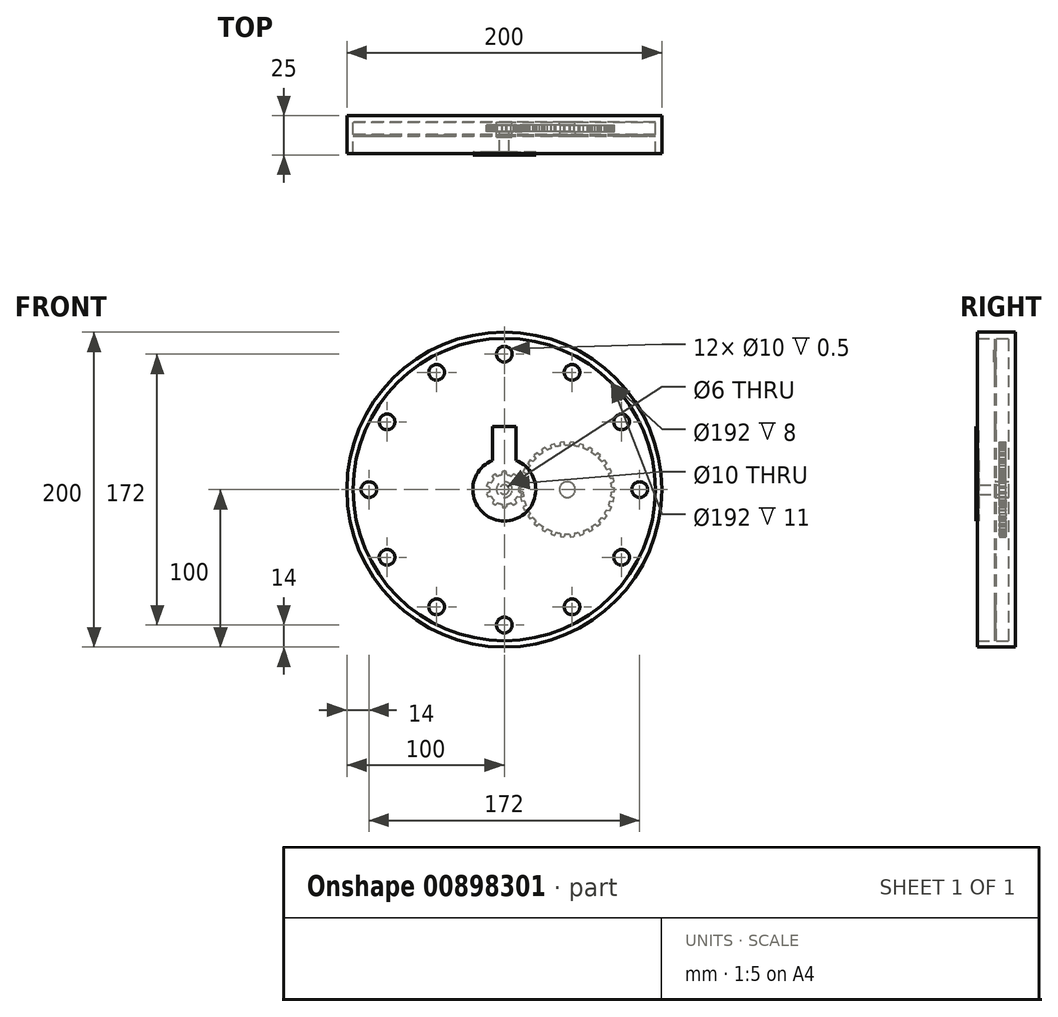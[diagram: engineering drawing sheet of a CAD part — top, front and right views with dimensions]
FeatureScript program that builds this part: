
annotation { "Feature Type Name" : "Feature", "Feature Type Description" : "" }
export const myFeature = defineFeature(function(context is Context, id is Id, definition is map)
    precondition{}
    {
        {
            var Q0;
            Q0=qCreatedBy(makeId("Front.planeOp"),FACE);
            var sketch = newSketch(context, id + "F0", { "sketchPlane" : qUnion([Q0])});
            skCircle(sketch, "E0", {"center": v(0, 0) * mm, "radius": 100 * mm});
            skSolve(sketch);
        }
        {
            var Q0;
            Q0=makeQuery(id+"F0.imprint","IMPRINT",FACE,{"disambiguationData":[TD([[makeQuery(id+"F0.imprint","IMPRINT",EDGE,{"derivedFrom":sQuery(id+"F0.wireOp",EDGE,"E0")}),1.0]])]});
            extrude(context, id + "F1", {"entities" : qUnion([Q0]), "depth" : 24 * mm, "offsetDistance" : 25 * mm});
        }
        {
            var Q0;
            Q0=makeQuery(id+"F1.opExtrude","CAP_FACE",FACE,{"disambiguationData":[OSD([sQuery(id+"F0.wireOp",EDGE,"E0")])],"isStart":false});
            shell(context, id + "F2", {"entities" : qUnion([Q0]), "thickness" : 4 * mm});
        }
        {
            var Q0;
            Q0=qCreatedBy(makeId("Front.planeOp"),FACE);
            var sketch = newSketch(context, id + "F3", { "sketchPlane" : qUnion([Q0])});
            skCircle(sketch, "E1", {"center": v(40, 0) * mm, "radius": 3 * mm});
            skCircle(sketch, "E2", {"center": v(40, 0) * mm, "radius": 5 * mm});
            skCircle(sketch, "E3", {"center": v(0, 0) * mm, "radius": 3 * mm});
            skCircle(sketch, "E4", {"center": v(0, 0) * mm, "radius": 5 * mm});
            skSolve(sketch);
        }
        {
            var Q0;
            Q0 = qSketchRegion(id + "F3", true);
            extrude(context, id + "F4", {"entities" : qUnion([Q0]), "operationType" : NewBodyOperationType.ADD, "depth" : 6 * mm, "offsetDistance" : 25 * mm});
        }
        {
            var Q0;
            {var subQ0=sQuery(id+"F0.wireOp",EDGE,"E0");Q0=makeQuery(id+"F4.boolean.opBoolean","SPLIT",FACE,{"disambiguationData":[TD([makeQuery(id+"F4.opExtrude","SWEPT_FACE",FACE,{"disambiguationData":[OSD([sQuery(id+"F3.wireOp",EDGE,"E3")])]})])],"derivedFrom":makeQuery(id+"F2.opShell","OFFSET_FACE",FACE,{"disambiguationData":[OSD([subQ0]),TDD([makeQuery(id+"F1.opExtrude","CAP_FACE",FACE,{"disambiguationData":[OSD([subQ0])],"isStart":true})])]})});}
            extrude(context, id + "F5", {"entities" : qUnion([Q0]), "depth" : 19 * mm, "offsetDistance" : 25 * mm});
        }
        {
            var Q0;
            {var subQ0=sQuery(id+"F0.wireOp",EDGE,"E0");Q0=makeQuery(id+"F4.boolean.opBoolean","SPLIT",FACE,{"disambiguationData":[TD([makeQuery(id+"F4.opExtrude","SWEPT_FACE",FACE,{"disambiguationData":[OSD([sQuery(id+"F3.wireOp",EDGE,"E1")])]})])],"derivedFrom":makeQuery(id+"F2.opShell","OFFSET_FACE",FACE,{"disambiguationData":[OSD([subQ0]),TDD([makeQuery(id+"F1.opExtrude","CAP_FACE",FACE,{"disambiguationData":[OSD([subQ0])],"isStart":true})])]})});}
            extrude(context, id + "F6", {"entities" : qUnion([Q0]), "depth" : 8 * mm, "offsetDistance" : 25 * mm});
        }
        {
            var Q0;
            Q0=makeQuery(id+"F4.opExtrude","CAP_FACE",FACE,{"disambiguationData":[OSD([sQuery(id+"F3.wireOp",EDGE,"E3"),sQuery(id+"F3.wireOp",EDGE,"E4")])],"isStart":false});
            var sketch = newSketch(context, id + "F7", { "sketchPlane" : qUnion([Q0])});
            skCircle(sketch, "E5", {"center": v(0, 0) * mm, "radius": 9.38 * mm});
            skLineSegment(sketch, "E6", {"start": v(1.55, 9.25) * mm, "end": v(1.18, 11.38) * mm});
            skLineSegment(sketch, "E7", {"start": v(1.18, 11.38) * mm, "end": v(0, 11.38) * mm});
            skLineSegment(sketch, "E8.MirrorCS", {"start": v(-1.18, 11.38) * mm, "end": v(0, 11.38) * mm});
            skLineSegment(sketch, "E9.MirrorCS", {"start": v(-1.55, 9.25) * mm, "end": v(-1.18, 11.38) * mm});
            skLineSegment(sketch, "E10.1.0", {"start": v(-6.7, 6.57) * mm, "end": v(-7.64, 8.51) * mm});
            skLineSegment(sketch, "E10.1.1", {"start": v(-7.64, 8.51) * mm, "end": v(-6.69, 9.2) * mm});
            skLineSegment(sketch, "E10.1.2", {"start": v(-5.73, 9.9) * mm, "end": v(-6.69, 9.2) * mm});
            skLineSegment(sketch, "E10.1.3", {"start": v(-4.18, 8.4) * mm, "end": v(-5.73, 9.9) * mm});
            skLineSegment(sketch, "E10.2.0", {"start": v(-9.27, 1.38) * mm, "end": v(-11.18, 2.4) * mm});
            skLineSegment(sketch, "E10.2.1", {"start": v(-11.18, 2.4) * mm, "end": v(-10.82, 3.52) * mm});
            skLineSegment(sketch, "E10.2.2", {"start": v(-10.45, 4.64) * mm, "end": v(-10.82, 3.52) * mm});
            skLineSegment(sketch, "E10.2.3", {"start": v(-8.31, 4.33) * mm, "end": v(-10.45, 4.64) * mm});
            skLineSegment(sketch, "E10.3.0", {"start": v(-8.31, -4.33) * mm, "end": v(-10.45, -4.64) * mm});
            skLineSegment(sketch, "E10.3.1", {"start": v(-10.45, -4.64) * mm, "end": v(-10.82, -3.52) * mm});
            skLineSegment(sketch, "E10.3.2", {"start": v(-11.18, -2.4) * mm, "end": v(-10.82, -3.52) * mm});
            skLineSegment(sketch, "E10.3.3", {"start": v(-9.27, -1.38) * mm, "end": v(-11.18, -2.4) * mm});
            skLineSegment(sketch, "E10.4.0", {"start": v(-4.18, -8.4) * mm, "end": v(-5.73, -9.9) * mm});
            skLineSegment(sketch, "E10.4.1", {"start": v(-5.73, -9.9) * mm, "end": v(-6.69, -9.2) * mm});
            skLineSegment(sketch, "E10.4.2", {"start": v(-7.64, -8.51) * mm, "end": v(-6.69, -9.2) * mm});
            skLineSegment(sketch, "E10.4.3", {"start": v(-6.7, -6.57) * mm, "end": v(-7.64, -8.51) * mm});
            skLineSegment(sketch, "E10.5.0", {"start": v(1.55, -9.25) * mm, "end": v(1.18, -11.38) * mm});
            skLineSegment(sketch, "E10.5.1", {"start": v(1.18, -11.38) * mm, "end": v(0, -11.38) * mm});
            skLineSegment(sketch, "E10.5.2", {"start": v(-1.18, -11.38) * mm, "end": v(0, -11.38) * mm});
            skLineSegment(sketch, "E10.5.3", {"start": v(-1.55, -9.25) * mm, "end": v(-1.18, -11.38) * mm});
            skLineSegment(sketch, "E10.6.0", {"start": v(6.7, -6.57) * mm, "end": v(7.64, -8.51) * mm});
            skLineSegment(sketch, "E10.6.1", {"start": v(7.64, -8.51) * mm, "end": v(6.69, -9.2) * mm});
            skLineSegment(sketch, "E10.6.2", {"start": v(5.73, -9.9) * mm, "end": v(6.69, -9.2) * mm});
            skLineSegment(sketch, "E10.6.3", {"start": v(4.18, -8.4) * mm, "end": v(5.73, -9.9) * mm});
            skLineSegment(sketch, "E10.7.0", {"start": v(9.27, -1.38) * mm, "end": v(11.18, -2.4) * mm});
            skLineSegment(sketch, "E10.7.1", {"start": v(11.18, -2.4) * mm, "end": v(10.82, -3.52) * mm});
            skLineSegment(sketch, "E10.7.2", {"start": v(10.45, -4.64) * mm, "end": v(10.82, -3.52) * mm});
            skLineSegment(sketch, "E10.7.3", {"start": v(8.31, -4.33) * mm, "end": v(10.45, -4.64) * mm});
            skLineSegment(sketch, "E10.8.0", {"start": v(8.31, 4.33) * mm, "end": v(10.45, 4.64) * mm});
            skLineSegment(sketch, "E10.8.1", {"start": v(10.45, 4.64) * mm, "end": v(10.82, 3.52) * mm});
            skLineSegment(sketch, "E10.8.2", {"start": v(11.18, 2.4) * mm, "end": v(10.82, 3.52) * mm});
            skLineSegment(sketch, "E10.8.3", {"start": v(9.27, 1.38) * mm, "end": v(11.18, 2.4) * mm});
            skLineSegment(sketch, "E10.9.0", {"start": v(4.18, 8.4) * mm, "end": v(5.73, 9.9) * mm});
            skLineSegment(sketch, "E10.9.1", {"start": v(5.73, 9.9) * mm, "end": v(6.69, 9.2) * mm});
            skLineSegment(sketch, "E10.9.2", {"start": v(7.64, 8.51) * mm, "end": v(6.69, 9.2) * mm});
            skLineSegment(sketch, "E10.9.3", {"start": v(6.7, 6.57) * mm, "end": v(7.64, 8.51) * mm});
            skSolve(sketch);
        }
        {
            var Q0;
            Q0 = qSketchRegion(id + "F7", true);
            extrude(context, id + "F8", {"entities" : qUnion([Q0]), "operationType" : NewBodyOperationType.ADD, "depth" : 4 * mm, "offsetDistance" : 25 * mm});
        }
        {
            var Q0;
            Q0=makeQuery(id+"F4.opExtrude","CAP_FACE",FACE,{"disambiguationData":[OSD([sQuery(id+"F3.wireOp",EDGE,"E1"),sQuery(id+"F3.wireOp",EDGE,"E2")])],"isStart":false});
            var sketch = newSketch(context, id + "F9", { "sketchPlane" : qUnion([Q0])});
            skCircle(sketch, "E11", {"center": v(40, 0) * mm, "radius": 28.12 * mm});
            skLineSegment(sketch, "E12", {"start": v(11.92, 1.54) * mm, "end": v(9.88, 1.18) * mm});
            skLineSegment(sketch, "E13", {"start": v(9.88, 1.18) * mm, "end": v(9.88, 0) * mm});
            skLineSegment(sketch, "E14.MirrorCS", {"start": v(9.88, -1.18) * mm, "end": v(9.88, 0) * mm});
            skLineSegment(sketch, "E15.MirrorCS", {"start": v(11.92, -1.54) * mm, "end": v(9.88, -1.18) * mm});
            skLineSegment(sketch, "E16.1.0", {"start": v(12.85, -7.34) * mm, "end": v(10.78, -7.42) * mm});
            skLineSegment(sketch, "E16.1.1", {"start": v(12.21, -4.33) * mm, "end": v(10.29, -5.11) * mm});
            skLineSegment(sketch, "E16.1.2", {"start": v(10.29, -5.11) * mm, "end": v(10.53, -6.26) * mm});
            skLineSegment(sketch, "E16.1.3", {"start": v(10.78, -7.42) * mm, "end": v(10.53, -6.26) * mm});
            skLineSegment(sketch, "E16.2.0", {"start": v(14.97, -12.83) * mm, "end": v(12.96, -13.33) * mm});
            skLineSegment(sketch, "E16.2.1", {"start": v(13.72, -10.02) * mm, "end": v(12, -11.18) * mm});
            skLineSegment(sketch, "E16.2.2", {"start": v(12, -11.18) * mm, "end": v(12.48, -12.25) * mm});
            skLineSegment(sketch, "E16.2.3", {"start": v(12.96, -13.33) * mm, "end": v(12.48, -12.25) * mm});
            skLineSegment(sketch, "E16.3.0", {"start": v(18.18, -17.75) * mm, "end": v(16.32, -18.66) * mm});
            skLineSegment(sketch, "E16.3.1", {"start": v(16.38, -15.26) * mm, "end": v(14.94, -16.75) * mm});
            skLineSegment(sketch, "E16.3.2", {"start": v(14.94, -16.75) * mm, "end": v(15.63, -17.7) * mm});
            skLineSegment(sketch, "E16.3.3", {"start": v(16.32, -18.66) * mm, "end": v(15.63, -17.7) * mm});
            skLineSegment(sketch, "E16.4.0", {"start": v(22.35, -21.9) * mm, "end": v(20.72, -23.18) * mm});
            skLineSegment(sketch, "E16.4.1", {"start": v(20.07, -19.84) * mm, "end": v(18.97, -21.6) * mm});
            skLineSegment(sketch, "E16.4.2", {"start": v(18.97, -21.6) * mm, "end": v(19.84, -22.39) * mm});
            skLineSegment(sketch, "E16.4.3", {"start": v(20.72, -23.18) * mm, "end": v(19.84, -22.39) * mm});
            skLineSegment(sketch, "E16.5.0", {"start": v(27.3, -25.09) * mm, "end": v(25.96, -26.68) * mm});
            skLineSegment(sketch, "E16.5.1", {"start": v(24.63, -23.55) * mm, "end": v(23.92, -25.5) * mm});
            skLineSegment(sketch, "E16.5.2", {"start": v(23.92, -25.5) * mm, "end": v(24.94, -26.09) * mm});
            skLineSegment(sketch, "E16.5.3", {"start": v(25.96, -26.68) * mm, "end": v(24.94, -26.09) * mm});
            skLineSegment(sketch, "E16.6.0", {"start": v(32.78, -27.18) * mm, "end": v(31.81, -29.01) * mm});
            skLineSegment(sketch, "E16.6.1", {"start": v(29.86, -26.23) * mm, "end": v(29.57, -28.29) * mm});
            skLineSegment(sketch, "E16.6.2", {"start": v(29.57, -28.29) * mm, "end": v(30.7, -28.65) * mm});
            skLineSegment(sketch, "E16.6.3", {"start": v(31.81, -29.01) * mm, "end": v(30.7, -28.65) * mm});
            skLineSegment(sketch, "E16.7.0", {"start": v(38.6, -28.09) * mm, "end": v(38.02, -30.08) * mm});
            skLineSegment(sketch, "E16.7.1", {"start": v(35.53, -27.77) * mm, "end": v(35.68, -29.84) * mm});
            skLineSegment(sketch, "E16.7.2", {"start": v(35.68, -29.84) * mm, "end": v(36.85, -29.96) * mm});
            skLineSegment(sketch, "E16.7.3", {"start": v(38.02, -30.08) * mm, "end": v(36.85, -29.96) * mm});
            skLineSegment(sketch, "E16.8.0", {"start": v(44.47, -27.77) * mm, "end": v(44.32, -29.84) * mm});
            skLineSegment(sketch, "E16.8.1", {"start": v(41.4, -28.09) * mm, "end": v(41.98, -30.08) * mm});
            skLineSegment(sketch, "E16.8.2", {"start": v(41.98, -30.08) * mm, "end": v(43.15, -29.96) * mm});
            skLineSegment(sketch, "E16.8.3", {"start": v(44.32, -29.84) * mm, "end": v(43.15, -29.96) * mm});
            skLineSegment(sketch, "E16.9.0", {"start": v(50.14, -26.23) * mm, "end": v(50.43, -28.29) * mm});
            skLineSegment(sketch, "E16.9.1", {"start": v(47.22, -27.18) * mm, "end": v(48.19, -29.01) * mm});
            skLineSegment(sketch, "E16.9.2", {"start": v(48.19, -29.01) * mm, "end": v(49.3, -28.65) * mm});
            skLineSegment(sketch, "E16.9.3", {"start": v(50.43, -28.29) * mm, "end": v(49.3, -28.65) * mm});
            skLineSegment(sketch, "E16.10.0", {"start": v(55.37, -23.55) * mm, "end": v(56.08, -25.5) * mm});
            skLineSegment(sketch, "E16.10.1", {"start": v(52.7, -25.09) * mm, "end": v(54.04, -26.68) * mm});
            skLineSegment(sketch, "E16.10.2", {"start": v(54.04, -26.68) * mm, "end": v(55.06, -26.09) * mm});
            skLineSegment(sketch, "E16.10.3", {"start": v(56.08, -25.5) * mm, "end": v(55.06, -26.09) * mm});
            skLineSegment(sketch, "E16.11.0", {"start": v(59.93, -19.84) * mm, "end": v(61.03, -21.6) * mm});
            skLineSegment(sketch, "E16.11.1", {"start": v(57.65, -21.9) * mm, "end": v(59.28, -23.18) * mm});
            skLineSegment(sketch, "E16.11.2", {"start": v(59.28, -23.18) * mm, "end": v(60.16, -22.39) * mm});
            skLineSegment(sketch, "E16.11.3", {"start": v(61.03, -21.6) * mm, "end": v(60.16, -22.39) * mm});
            skLineSegment(sketch, "E16.12.0", {"start": v(63.62, -15.26) * mm, "end": v(65.06, -16.75) * mm});
            skLineSegment(sketch, "E16.12.1", {"start": v(61.82, -17.75) * mm, "end": v(63.68, -18.66) * mm});
            skLineSegment(sketch, "E16.12.2", {"start": v(63.68, -18.66) * mm, "end": v(64.37, -17.7) * mm});
            skLineSegment(sketch, "E16.12.3", {"start": v(65.06, -16.75) * mm, "end": v(64.37, -17.7) * mm});
            skLineSegment(sketch, "E16.13.0", {"start": v(66.28, -10.02) * mm, "end": v(68, -11.18) * mm});
            skLineSegment(sketch, "E16.13.1", {"start": v(65.03, -12.83) * mm, "end": v(67.04, -13.33) * mm});
            skLineSegment(sketch, "E16.13.2", {"start": v(67.04, -13.33) * mm, "end": v(67.52, -12.25) * mm});
            skLineSegment(sketch, "E16.13.3", {"start": v(68, -11.18) * mm, "end": v(67.52, -12.25) * mm});
            skLineSegment(sketch, "E16.14.0", {"start": v(67.79, -4.33) * mm, "end": v(69.71, -5.11) * mm});
            skLineSegment(sketch, "E16.14.1", {"start": v(67.15, -7.34) * mm, "end": v(69.22, -7.42) * mm});
            skLineSegment(sketch, "E16.14.2", {"start": v(69.22, -7.42) * mm, "end": v(69.47, -6.26) * mm});
            skLineSegment(sketch, "E16.14.3", {"start": v(69.71, -5.11) * mm, "end": v(69.47, -6.26) * mm});
            skLineSegment(sketch, "E16.15.0", {"start": v(68.08, 1.54) * mm, "end": v(70.12, 1.18) * mm});
            skLineSegment(sketch, "E16.15.1", {"start": v(68.08, -1.54) * mm, "end": v(70.12, -1.18) * mm});
            skLineSegment(sketch, "E16.15.2", {"start": v(70.12, -1.18) * mm, "end": v(70.12, 0) * mm});
            skLineSegment(sketch, "E16.15.3", {"start": v(70.12, 1.18) * mm, "end": v(70.12, 0) * mm});
            skLineSegment(sketch, "E16.16.0", {"start": v(67.15, 7.34) * mm, "end": v(69.22, 7.42) * mm});
            skLineSegment(sketch, "E16.16.1", {"start": v(67.79, 4.33) * mm, "end": v(69.71, 5.11) * mm});
            skLineSegment(sketch, "E16.16.2", {"start": v(69.71, 5.11) * mm, "end": v(69.47, 6.26) * mm});
            skLineSegment(sketch, "E16.16.3", {"start": v(69.22, 7.42) * mm, "end": v(69.47, 6.26) * mm});
            skLineSegment(sketch, "E16.17.0", {"start": v(65.03, 12.83) * mm, "end": v(67.04, 13.33) * mm});
            skLineSegment(sketch, "E16.17.1", {"start": v(66.28, 10.02) * mm, "end": v(68, 11.18) * mm});
            skLineSegment(sketch, "E16.17.2", {"start": v(68, 11.18) * mm, "end": v(67.52, 12.25) * mm});
            skLineSegment(sketch, "E16.17.3", {"start": v(67.04, 13.33) * mm, "end": v(67.52, 12.25) * mm});
            skLineSegment(sketch, "E16.18.0", {"start": v(61.82, 17.75) * mm, "end": v(63.68, 18.66) * mm});
            skLineSegment(sketch, "E16.18.1", {"start": v(63.62, 15.26) * mm, "end": v(65.06, 16.75) * mm});
            skLineSegment(sketch, "E16.18.2", {"start": v(65.06, 16.75) * mm, "end": v(64.37, 17.7) * mm});
            skLineSegment(sketch, "E16.18.3", {"start": v(63.68, 18.66) * mm, "end": v(64.37, 17.7) * mm});
            skLineSegment(sketch, "E16.19.0", {"start": v(57.65, 21.9) * mm, "end": v(59.28, 23.18) * mm});
            skLineSegment(sketch, "E16.19.1", {"start": v(59.93, 19.84) * mm, "end": v(61.03, 21.6) * mm});
            skLineSegment(sketch, "E16.19.2", {"start": v(61.03, 21.6) * mm, "end": v(60.16, 22.39) * mm});
            skLineSegment(sketch, "E16.19.3", {"start": v(59.28, 23.18) * mm, "end": v(60.16, 22.39) * mm});
            skLineSegment(sketch, "E16.20.0", {"start": v(52.7, 25.09) * mm, "end": v(54.04, 26.68) * mm});
            skLineSegment(sketch, "E16.20.1", {"start": v(55.37, 23.55) * mm, "end": v(56.08, 25.5) * mm});
            skLineSegment(sketch, "E16.20.2", {"start": v(56.08, 25.5) * mm, "end": v(55.06, 26.09) * mm});
            skLineSegment(sketch, "E16.20.3", {"start": v(54.04, 26.68) * mm, "end": v(55.06, 26.09) * mm});
            skLineSegment(sketch, "E16.21.0", {"start": v(47.22, 27.18) * mm, "end": v(48.19, 29.01) * mm});
            skLineSegment(sketch, "E16.21.1", {"start": v(50.14, 26.23) * mm, "end": v(50.43, 28.29) * mm});
            skLineSegment(sketch, "E16.21.2", {"start": v(50.43, 28.29) * mm, "end": v(49.3, 28.65) * mm});
            skLineSegment(sketch, "E16.21.3", {"start": v(48.19, 29.01) * mm, "end": v(49.3, 28.65) * mm});
            skLineSegment(sketch, "E16.22.0", {"start": v(41.4, 28.09) * mm, "end": v(41.98, 30.08) * mm});
            skLineSegment(sketch, "E16.22.1", {"start": v(44.47, 27.77) * mm, "end": v(44.32, 29.84) * mm});
            skLineSegment(sketch, "E16.22.2", {"start": v(44.32, 29.84) * mm, "end": v(43.15, 29.96) * mm});
            skLineSegment(sketch, "E16.22.3", {"start": v(41.98, 30.08) * mm, "end": v(43.15, 29.96) * mm});
            skLineSegment(sketch, "E16.23.0", {"start": v(35.53, 27.77) * mm, "end": v(35.68, 29.84) * mm});
            skLineSegment(sketch, "E16.23.1", {"start": v(38.6, 28.09) * mm, "end": v(38.02, 30.08) * mm});
            skLineSegment(sketch, "E16.23.2", {"start": v(38.02, 30.08) * mm, "end": v(36.85, 29.96) * mm});
            skLineSegment(sketch, "E16.23.3", {"start": v(35.68, 29.84) * mm, "end": v(36.85, 29.96) * mm});
            skLineSegment(sketch, "E16.24.0", {"start": v(29.86, 26.23) * mm, "end": v(29.57, 28.29) * mm});
            skLineSegment(sketch, "E16.24.1", {"start": v(32.78, 27.18) * mm, "end": v(31.81, 29.01) * mm});
            skLineSegment(sketch, "E16.24.2", {"start": v(31.81, 29.01) * mm, "end": v(30.7, 28.65) * mm});
            skLineSegment(sketch, "E16.24.3", {"start": v(29.57, 28.29) * mm, "end": v(30.7, 28.65) * mm});
            skLineSegment(sketch, "E16.25.0", {"start": v(24.63, 23.55) * mm, "end": v(23.92, 25.5) * mm});
            skLineSegment(sketch, "E16.25.1", {"start": v(27.3, 25.09) * mm, "end": v(25.96, 26.68) * mm});
            skLineSegment(sketch, "E16.25.2", {"start": v(25.96, 26.68) * mm, "end": v(24.94, 26.09) * mm});
            skLineSegment(sketch, "E16.25.3", {"start": v(23.92, 25.5) * mm, "end": v(24.94, 26.09) * mm});
            skLineSegment(sketch, "E16.26.0", {"start": v(20.07, 19.84) * mm, "end": v(18.97, 21.6) * mm});
            skLineSegment(sketch, "E16.26.1", {"start": v(22.35, 21.9) * mm, "end": v(20.72, 23.18) * mm});
            skLineSegment(sketch, "E16.26.2", {"start": v(20.72, 23.18) * mm, "end": v(19.84, 22.39) * mm});
            skLineSegment(sketch, "E16.26.3", {"start": v(18.97, 21.6) * mm, "end": v(19.84, 22.39) * mm});
            skLineSegment(sketch, "E16.27.0", {"start": v(16.38, 15.26) * mm, "end": v(14.94, 16.75) * mm});
            skLineSegment(sketch, "E16.27.1", {"start": v(18.18, 17.75) * mm, "end": v(16.32, 18.66) * mm});
            skLineSegment(sketch, "E16.27.2", {"start": v(16.32, 18.66) * mm, "end": v(15.63, 17.7) * mm});
            skLineSegment(sketch, "E16.27.3", {"start": v(14.94, 16.75) * mm, "end": v(15.63, 17.7) * mm});
            skLineSegment(sketch, "E16.28.0", {"start": v(13.72, 10.02) * mm, "end": v(12, 11.18) * mm});
            skLineSegment(sketch, "E16.28.1", {"start": v(14.97, 12.83) * mm, "end": v(12.96, 13.33) * mm});
            skLineSegment(sketch, "E16.28.2", {"start": v(12.96, 13.33) * mm, "end": v(12.48, 12.25) * mm});
            skLineSegment(sketch, "E16.28.3", {"start": v(12, 11.18) * mm, "end": v(12.48, 12.25) * mm});
            skLineSegment(sketch, "E16.29.0", {"start": v(12.21, 4.33) * mm, "end": v(10.29, 5.11) * mm});
            skLineSegment(sketch, "E16.29.1", {"start": v(12.85, 7.34) * mm, "end": v(10.78, 7.42) * mm});
            skLineSegment(sketch, "E16.29.2", {"start": v(10.78, 7.42) * mm, "end": v(10.53, 6.26) * mm});
            skLineSegment(sketch, "E16.29.3", {"start": v(10.29, 5.11) * mm, "end": v(10.53, 6.26) * mm});
            skSolve(sketch);
        }
        {
            var Q0;
            Q0 = qSketchRegion(id + "F9", true);
            extrude(context, id + "F10", {"entities" : qUnion([Q0]), "operationType" : NewBodyOperationType.ADD, "depth" : 4 * mm, "offsetDistance" : 25 * mm});
        }
        {
            var Q0;
            Q0=makeQuery(id+"F8.opExtrude","CAP_FACE",FACE,{"disambiguationData":[OSD([sQuery(id+"F7.wireOp",EDGE,"E5"),sQuery(id+"F7.wireOp",EDGE,"E6"),sQuery(id+"F7.wireOp",EDGE,"E7"),sQuery(id+"F7.wireOp",EDGE,"E8.MirrorCS"),sQuery(id+"F7.wireOp",EDGE,"E9.MirrorCS"),sQuery(id+"F7.wireOp",EDGE,"E10.1.0"),sQuery(id+"F7.wireOp",EDGE,"E10.1.1"),sQuery(id+"F7.wireOp",EDGE,"E10.1.2"),sQuery(id+"F7.wireOp",EDGE,"E10.1.3"),sQuery(id+"F7.wireOp",EDGE,"E10.2.0"),sQuery(id+"F7.wireOp",EDGE,"E10.2.1"),sQuery(id+"F7.wireOp",EDGE,"E10.2.2"),sQuery(id+"F7.wireOp",EDGE,"E10.2.3"),sQuery(id+"F7.wireOp",EDGE,"E10.3.0"),sQuery(id+"F7.wireOp",EDGE,"E10.3.1"),sQuery(id+"F7.wireOp",EDGE,"E10.3.2"),sQuery(id+"F7.wireOp",EDGE,"E10.3.3"),sQuery(id+"F7.wireOp",EDGE,"E10.4.0"),sQuery(id+"F7.wireOp",EDGE,"E10.4.1"),sQuery(id+"F7.wireOp",EDGE,"E10.4.2"),sQuery(id+"F7.wireOp",EDGE,"E10.4.3"),sQuery(id+"F7.wireOp",EDGE,"E10.5.0"),sQuery(id+"F7.wireOp",EDGE,"E10.5.1"),sQuery(id+"F7.wireOp",EDGE,"E10.5.2"),sQuery(id+"F7.wireOp",EDGE,"E10.5.3"),sQuery(id+"F7.wireOp",EDGE,"E10.6.0"),sQuery(id+"F7.wireOp",EDGE,"E10.6.1"),sQuery(id+"F7.wireOp",EDGE,"E10.6.2"),sQuery(id+"F7.wireOp",EDGE,"E10.6.3"),sQuery(id+"F7.wireOp",EDGE,"E10.7.0"),sQuery(id+"F7.wireOp",EDGE,"E10.7.1"),sQuery(id+"F7.wireOp",EDGE,"E10.7.2"),sQuery(id+"F7.wireOp",EDGE,"E10.7.3"),sQuery(id+"F7.wireOp",EDGE,"E10.8.0"),sQuery(id+"F7.wireOp",EDGE,"E10.8.1"),sQuery(id+"F7.wireOp",EDGE,"E10.8.2"),sQuery(id+"F7.wireOp",EDGE,"E10.8.3"),sQuery(id+"F7.wireOp",EDGE,"E10.9.0"),sQuery(id+"F7.wireOp",EDGE,"E10.9.1"),sQuery(id+"F7.wireOp",EDGE,"E10.9.2"),sQuery(id+"F7.wireOp",EDGE,"E10.9.3")])],"isStart":false});
            var sketch = newSketch(context, id + "F11", { "sketchPlane" : qUnion([Q0])});
            skCircle(sketch, "E17.0", {"center": v(0, 0) * mm, "radius": 3 * mm});
            skCircle(sketch, "E18.0", {"center": v(0, 0) * mm, "radius": 5 * mm});
            skSolve(sketch);
        }
        {
            var Q0;
            Q0 = qSketchRegion(id + "F11", true);
            extrude(context, id + "F12", {"entities" : qUnion([Q0]), "depth" : 2 * mm, "offsetDistance" : 25 * mm});
        }
        {
            var Q0;
            Q0=makeQuery(id+"F6.opExtrude","CAP_FACE",FACE,{"disambiguationData":[OSD([sQuery(id+"F0.wireOp",EDGE,"E0")])],"isStart":false});
            var sketch = newSketch(context, id + "F13", { "sketchPlane" : qUnion([Q0])});
            skCircle(sketch, "E19", {"center": v(0, 0) * mm, "radius": 98 * mm});
            skCircle(sketch, "E20.0", {"center": v(0, 0) * mm, "radius": 5 * mm});
            skCircle(sketch, "E21.0", {"center": v(0, 0) * mm, "radius": 3 * mm});
            skSolve(sketch);
        }
        {
            var Q0;
            Q0 = qSketchRegion(id + "F13", true);
            extrude(context, id + "F14", {"entities" : qUnion([Q0]), "depth" : 1 * mm, "offsetDistance" : 25 * mm});
        }
        {
            var Q0;
            Q0=makeQuery(id+"F14.opExtrude","SWEPT_BODY",BODY,{"disambiguationData":[OSD([sQuery(id+"F13.wireOp",EDGE,"E19"),sQuery(id+"F13.wireOp",EDGE,"E20.0")])]});
            var Q1;
            Q1=makeQuery(id+"F1.opExtrude","SWEPT_BODY",BODY,{"disambiguationData":[OSD([sQuery(id+"F0.wireOp",EDGE,"E0")])]});
            booleanBodies(context, id + "F15", {"operationType" : BooleanOperationType.SUBTRACTION, "tools" : qUnion([Q0]), "targets" : qUnion([Q1]), "keepTools" : true});
        }
        {
            var Q0;
            Q0=makeQuery(id+"F14.opExtrude","CAP_FACE",FACE,{"disambiguationData":[OSD([sQuery(id+"F13.wireOp",EDGE,"E19"),sQuery(id+"F13.wireOp",EDGE,"E20.0")])],"isStart":true});
            var sketch = newSketch(context, id + "F16", { "sketchPlane" : qUnion([Q0])});
            skCircle(sketch, "E22.0.0", {"center": v(-40, 0) * mm, "radius": 3 * mm});
            skCircle(sketch, "E23", {"center": v(-40, 0) * mm, "radius": 5 * mm});
            skSolve(sketch);
        }
        {
            var Q0;
            Q0 = qSketchRegion(id + "F16", true);
            extrude(context, id + "F17", {"entities" : qUnion([Q0]), "operationType" : NewBodyOperationType.ADD, "endBound" : BoundingType.UP_TO_NEXT, "depth" : 25 * mm, "offsetDistance" : 25 * mm});
        }
        {
            var Q0;
            Q0=makeQuery(id+"F14.opExtrude","CAP_FACE",FACE,{"disambiguationData":[OSD([sQuery(id+"F13.wireOp",EDGE,"E19"),sQuery(id+"F13.wireOp",EDGE,"E20.0")])],"isStart":false});
            var sketch = newSketch(context, id + "F18", { "sketchPlane" : qUnion([Q0])});
            skCircle(sketch, "E24", {"center": v(0, 86) * mm, "radius": 5 * mm});
            skCircle(sketch, "E25.1.0", {"center": v(-43, 74.48) * mm, "radius": 5 * mm});
            skCircle(sketch, "E25.2.0", {"center": v(-74.48, 43) * mm, "radius": 5 * mm});
            skCircle(sketch, "E25.3.0", {"center": v(-86, 0) * mm, "radius": 5 * mm});
            skCircle(sketch, "E25.4.0", {"center": v(-74.48, -43) * mm, "radius": 5 * mm});
            skCircle(sketch, "E25.5.0", {"center": v(-43, -74.48) * mm, "radius": 5 * mm});
            skCircle(sketch, "E25.6.0", {"center": v(0, -86) * mm, "radius": 5 * mm});
            skCircle(sketch, "E25.7.0", {"center": v(43, -74.48) * mm, "radius": 5 * mm});
            skCircle(sketch, "E25.8.0", {"center": v(74.48, -43) * mm, "radius": 5 * mm});
            skCircle(sketch, "E25.9.0", {"center": v(86, 0) * mm, "radius": 5 * mm});
            skCircle(sketch, "E25.10.0", {"center": v(74.48, 43) * mm, "radius": 5 * mm});
            skCircle(sketch, "E25.11.0", {"center": v(43, 74.48) * mm, "radius": 5 * mm});
            skPoint(sketch, "E25.center", {"position": v(0, 0) * mm});
            skSolve(sketch);
        }
        {
            var Q0;
            Q0 = qSketchRegion(id + "F18", true);
            extrude(context, id + "F19", {"entities" : qUnion([Q0]), "operationType" : NewBodyOperationType.REMOVE, "oppositeDirection" : true, "depth" : 0.5 * mm, "offsetDistance" : 25 * mm});
        }
        {
            var Q0;
            Q0=makeQuery(id+"F19.boolean.opBoolean","COPY",FACE,{"derivedFrom":makeQuery(id+"F19.opExtrude","CAP_FACE",FACE,{"disambiguationData":[OSD([sQuery(id+"F18.wireOp",EDGE,"E24")])],"isStart":false})});
            extrude(context, id + "F20", {"entities" : qUnion([Q0]), "depth" : 1 * mm, "offsetDistance" : 25 * mm});
        }
        {
            var Q0;
            Q0=makeQuery(id+"F5.opExtrude","CAP_FACE",FACE,{"disambiguationData":[OSD([sQuery(id+"F0.wireOp",EDGE,"E0")])],"isStart":false});
            var sketch = newSketch(context, id + "F21", { "sketchPlane" : qUnion([Q0])});
            skCircle(sketch, "E26", {"center": v(0, 0) * mm, "radius": 20 * mm});
            skLineSegment(sketch, "E27", {"start": v(-7.5, 18.54) * mm, "end": v(-7.5, 40) * mm});
            skLineSegment(sketch, "E28", {"start": v(-7.5, 40) * mm, "end": v(0, 40) * mm});
            skLineSegment(sketch, "E29.MirrorCS", {"start": v(7.5, 40) * mm, "end": v(0, 40) * mm});
            skLineSegment(sketch, "E30.MirrorCS", {"start": v(7.5, 18.54) * mm, "end": v(7.5, 40) * mm});
            skSolve(sketch);
        }
        {
            var Q0;
            Q0 = qSketchRegion(id + "F21", true);
            extrude(context, id + "F22", {"entities" : qUnion([Q0]), "operationType" : NewBodyOperationType.ADD, "depth" : 2 * mm, "offsetDistance" : 25 * mm});
        }
    });
